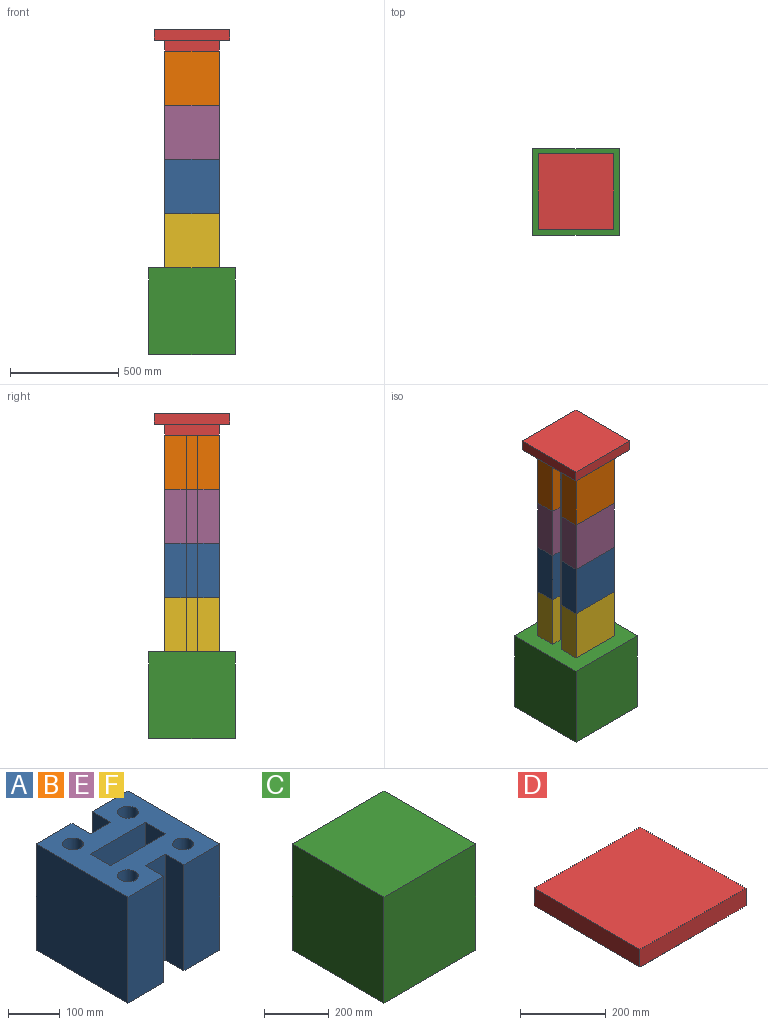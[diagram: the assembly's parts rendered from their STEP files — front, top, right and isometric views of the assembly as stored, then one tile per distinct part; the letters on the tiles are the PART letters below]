
ASSEMBLY  parts=6 mates=5
PART A: 22 faces, bbox 250x250x250 mm
  f0: plane 250x55mm, normal (-1,0,0), area 13750mm2, adj f1,f19,f20,f21
  f1: plane 250x150mm, normal (0,1,0), area 37500mm2, adj f0,f2,f20,f21
  f2: plane 250x55mm, normal (1,0,0), area 13750mm2, adj f1,f19,f20,f21
  f3: plane 250x50mm, normal (1,0,0), area 12500mm2, adj f4,f14,f20,f21
  f4: plane 250x97.5mm, normal (0,1,0), area 24375mm2, adj f3,f5,f20,f21
  f5: plane 250x250mm, normal (-1,0,0), area 62500mm2, adj f4,f6,f20,f21
  f6: plane 250x97.5mm, normal (0,-1,0), area 24375mm2, adj f5,f7,f20,f21
  f7: plane 250x50mm, normal (1,0,0), area 12500mm2, adj f6,f8,f20,f21
  f8: plane 250x55mm, normal (0,-1,0), area 13750mm2, adj f7,f9,f20,f21
  f9: plane 250x50mm, normal (-1,0,0), area 12500mm2, adj f8,f10,f20,f21
  f10: plane 250x97.5mm, normal (0,-1,0), area 24375mm2, adj f9,f11,f20,f21
  f11: plane 250x250mm, normal (1,0,0), area 62500mm2, adj f10,f12,f20,f21
  f12: plane 250x97.5mm, normal (0,1,0), area 24375mm2, adj f11,f13,f20,f21
  f13: plane 250x50mm, normal (-1,0,0), area 12500mm2, adj f12,f14,f20,f21
  f14: plane 250x55mm, normal (0,1,0), area 13750mm2, adj f3,f13,f20,f21
  f15: cylinder r=20mm len=250mm, axis (0,0,-1), area 31415.9mm2, adj f20,f21
  f16: cylinder r=20mm len=250mm, axis (0,0,-1), area 31415.9mm2, adj f20,f21
  f17: cylinder r=20mm len=250mm, axis (0,0,-1), area 31415.9mm2, adj f20,f21
  f18: cylinder r=20mm len=250mm, axis (0,0,-1), area 31415.9mm2, adj f20,f21
  f19: plane 250x150mm, normal (0,-1,0), area 37500mm2, adj f0,f2,f20,f21
  f20: plane 250x250mm, normal (0,0,1), area 43723.5mm2, adj f0,f1,f2,f3,f4,f5,f6,f7
  f21: plane 250x250mm, normal (0,0,-1), area 43723.5mm2, adj f0,f1,f2,f3,f4,f5,f6,f7
PART B: same geometry as A
PART C: 6 faces, bbox 400x400x400 mm
  f0: plane 400x400mm, normal (0,-1,0), area 160000mm2, adj f1,f3,f4,f5
  f1: plane 400x400mm, normal (1,0,0), area 160000mm2, adj f0,f2,f4,f5
  f2: plane 400x400mm, normal (0,1,0), area 160000mm2, adj f1,f3,f4,f5
  f3: plane 400x400mm, normal (-1,0,0), area 160000mm2, adj f0,f2,f4,f5
  f4: plane 400x400mm, normal (0,0,1), area 160000mm2, adj f0,f1,f2,f3
  f5: plane 400x400mm, normal (0,0,-1), area 160000mm2, adj f0,f1,f2,f3
PART D: 11 faces, bbox 350x350x100 mm
  f0: plane 350x50mm, normal (0,-1,0), area 17500mm2, adj f1,f3,f4,f5
  f1: plane 350x50mm, normal (1,0,0), area 17500mm2, adj f0,f2,f4,f5
  f2: plane 350x50mm, normal (0,1,0), area 17500mm2, adj f1,f3,f4,f5
  f3: plane 350x50mm, normal (-1,0,0), area 17500mm2, adj f0,f2,f4,f5
  f4: plane 350x350mm, normal (0,0,1), area 122500mm2, adj f0,f1,f2,f3
  f5: plane 350x350mm, normal (0,0,-1), area 60000mm2, adj f0,f1,f2,f3,f6,f7,f8,f9
  f6: plane 250x50mm, normal (1,0,0), area 12500mm2, adj f5,f7,f9,f10
  f7: plane 250x50mm, normal (0,1,0), area 12500mm2, adj f5,f6,f8,f10
  f8: plane 250x50mm, normal (-1,0,0), area 12500mm2, adj f5,f7,f9,f10
  f9: plane 250x50mm, normal (0,-1,0), area 12500mm2, adj f5,f6,f8,f10
  f10: plane 250x250mm, normal (0,0,-1), area 62500mm2, adj f6,f7,f8,f9
PART E: same geometry as A
PART F: same geometry as A
PLACE A rot(axis=(0,0,1),90deg) t=(78.71,175.29,375.43)mm
PLACE B rot(axis=(0,0,1),90deg) t=(78.71,175.29,875.43)mm
PLACE C t=(78.71,175.29,-199.57)mm fixed
PLACE D t=(78.71,175.29,1050.43)mm
PLACE E rot(axis=(0,0,1),90deg) t=(78.71,175.29,625.43)mm
PLACE F rot(axis=(0,0,1),90deg) t=(78.71,175.29,125.43)mm
MATE fastened E.f21 <-> A.f20  axis (0,0,-1) through (-46.29,50.29,500.43)mm
MATE fastened F.f21 <-> C.f4  axis (0,0,-1) through (78.71,175.29,0.43)mm
MATE fastened A.f21 <-> F.f20  axis (0,0,-1) through (-46.29,50.29,250.43)mm
MATE fastened B.f21 <-> E.f20  axis (0,0,-1) through (-46.29,50.29,750.43)mm
MATE fastened D.f10 <-> B.f20  axis (0,0,-1) through (-46.29,50.29,1000.43)mm
